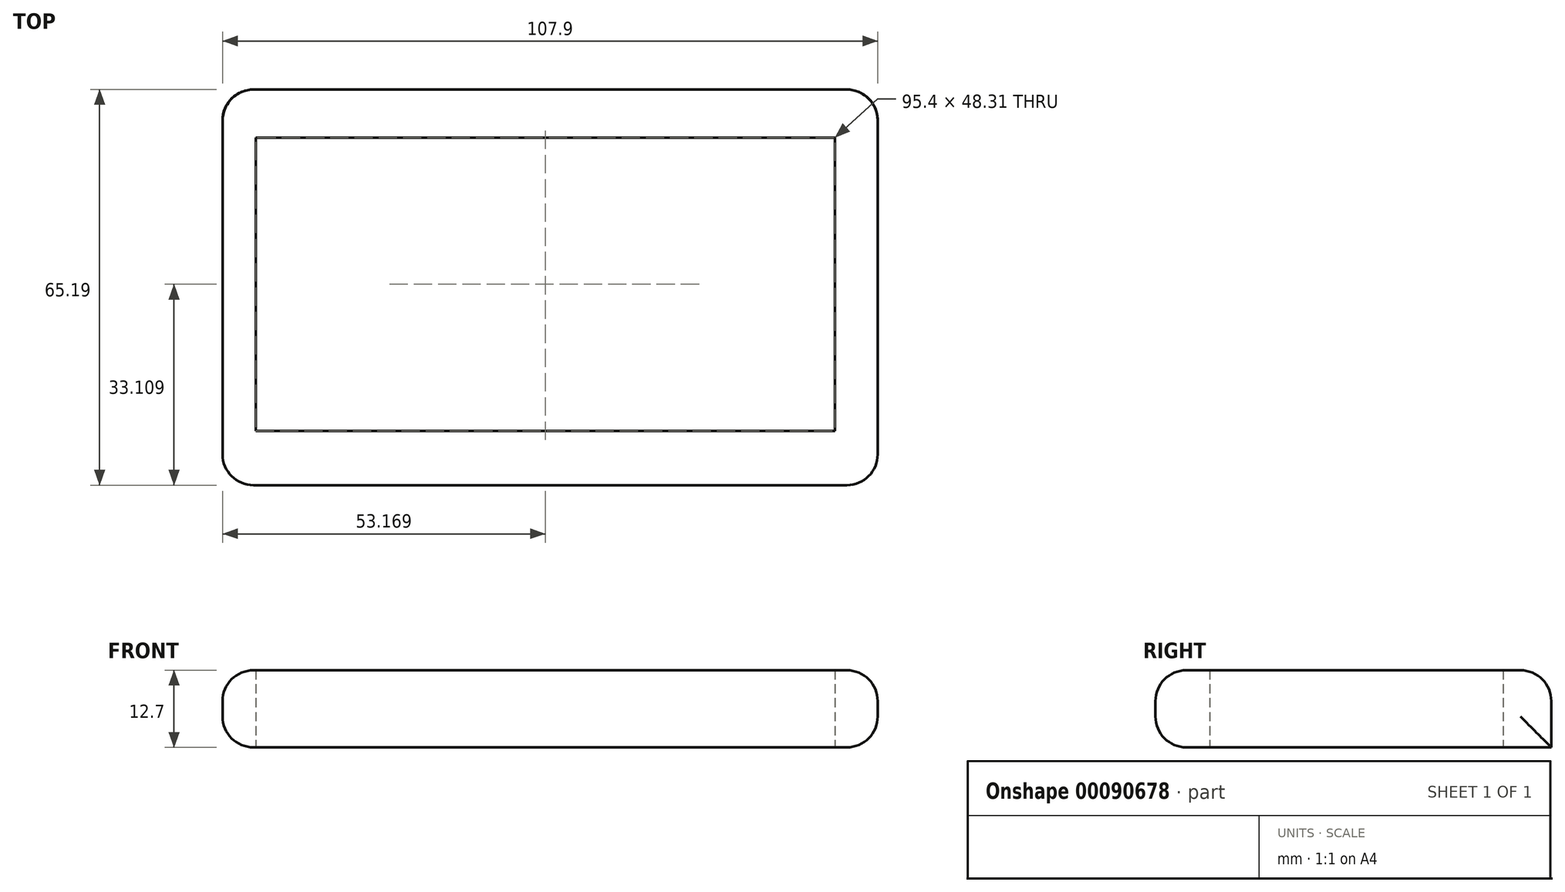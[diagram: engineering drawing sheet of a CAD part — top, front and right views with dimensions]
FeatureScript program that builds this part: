
annotation { "Feature Type Name" : "Feature", "Feature Type Description" : "" }
export const myFeature = defineFeature(function(context is Context, id is Id, definition is map)
    precondition{}
    {
        {
            var Q0;
            Q0=qCreatedBy(makeId("Top.planeOp"),FACE);
            var sketch = newSketch(context, id + "F0", { "sketchPlane" : qUnion([Q0])});
            skLineSegment(sketch, "E0.bottom", {"start": v(-51.44, -30.66) * mm, "end": v(56.46, -30.66) * mm});
            skLineSegment(sketch, "E0.top", {"start": v(-51.44, 34.53) * mm, "end": v(56.46, 34.53) * mm});
            skLineSegment(sketch, "E0.left", {"start": v(-51.44, -30.66) * mm, "end": v(-51.44, 34.53) * mm});
            skLineSegment(sketch, "E0.right", {"start": v(56.46, -30.66) * mm, "end": v(56.46, 34.53) * mm});
            skLineSegment(sketch, "E1.bottom", {"start": v(-45.97, -21.7) * mm, "end": v(49.43, -21.7) * mm});
            skLineSegment(sketch, "E1.top", {"start": v(-45.97, 26.6) * mm, "end": v(49.43, 26.6) * mm});
            skLineSegment(sketch, "E1.left", {"start": v(-45.97, -21.7) * mm, "end": v(-45.97, 26.6) * mm});
            skLineSegment(sketch, "E1.right", {"start": v(49.43, -21.7) * mm, "end": v(49.43, 26.6) * mm});
            skSolve(sketch);
        }
        {
            var Q0;
            Q0=makeQuery(id+"F0.imprint","IMPRINT",FACE,{"disambiguationData":[TD([[makeQuery(id+"F0.imprint","IMPRINT",EDGE,{"derivedFrom":sQuery(id+"F0.wireOp",EDGE,"E0.bottom")}),1.0]])]});
            extrude(context, id + "F1", {"entities" : qUnion([Q0]), "depth" : 12.7 * mm});
        }
        {
            var Q0;
            Q0=makeQuery(id+"F1.opExtrude","CAP_EDGE",EDGE,{"disambiguationData":[OSD([sQuery(id+"F0.wireOp",EDGE,"E0.bottom")])],"isStart":false});
            var Q1;
            Q1=makeQuery(id+"F1.opExtrude","CAP_EDGE",EDGE,{"disambiguationData":[OSD([sQuery(id+"F0.wireOp",EDGE,"E0.left")])],"isStart":false});
            var Q2;
            Q2=makeQuery(id+"F1.opExtrude","CAP_EDGE",EDGE,{"disambiguationData":[OSD([sQuery(id+"F0.wireOp",EDGE,"E0.top")])],"isStart":false});
            var Q3;
            Q3=makeQuery(id+"F1.opExtrude","CAP_EDGE",EDGE,{"disambiguationData":[OSD([sQuery(id+"F0.wireOp",EDGE,"E0.right")])],"isStart":false});
            var Q4;
            Q4=makeQuery(id+"F1.opExtrude","SWEPT_EDGE",EDGE,{"disambiguationData":[OSD([sQuery(id+"F0.wireOp",EDGE,"E0.bottom"),sQuery(id+"F0.wireOp",EDGE,"E0.right")])]});
            var Q5;
            Q5=makeQuery(id+"F1.opExtrude","CAP_EDGE",EDGE,{"disambiguationData":[OSD([sQuery(id+"F0.wireOp",EDGE,"E0.bottom")])],"isStart":true});
            var Q6;
            Q6=makeQuery(id+"F1.opExtrude","CAP_EDGE",EDGE,{"disambiguationData":[OSD([sQuery(id+"F0.wireOp",EDGE,"E0.right")])],"isStart":true});
            var Q7;
            Q7=makeQuery(id+"F1.opExtrude","SWEPT_EDGE",EDGE,{"disambiguationData":[OSD([sQuery(id+"F0.wireOp",EDGE,"E0.top"),sQuery(id+"F0.wireOp",EDGE,"E0.left")])]});
            var Q8;
            Q8=makeQuery(id+"F1.opExtrude","SWEPT_EDGE",EDGE,{"disambiguationData":[OSD([sQuery(id+"F0.wireOp",EDGE,"E0.bottom"),sQuery(id+"F0.wireOp",EDGE,"E0.left")])]});
            var Q9;
            Q9=makeQuery(id+"F1.opExtrude","CAP_EDGE",EDGE,{"disambiguationData":[OSD([sQuery(id+"F0.wireOp",EDGE,"E0.left")])],"isStart":true});
            var Q10;
            Q10=makeQuery(id+"F1.opExtrude","SWEPT_EDGE",EDGE,{"disambiguationData":[OSD([sQuery(id+"F0.wireOp",EDGE,"E0.top"),sQuery(id+"F0.wireOp",EDGE,"E0.right")])]});
            fillet(context, id + "F2", {"entities" : qUnion([Q0, Q1, Q2, Q3, Q4, Q5, Q6, Q7, Q8, Q9, Q10]), "radius" : 5.08 * mm, "tangentPropagation" : true, "allowEdgeOverflow" : false});
        }
    });
